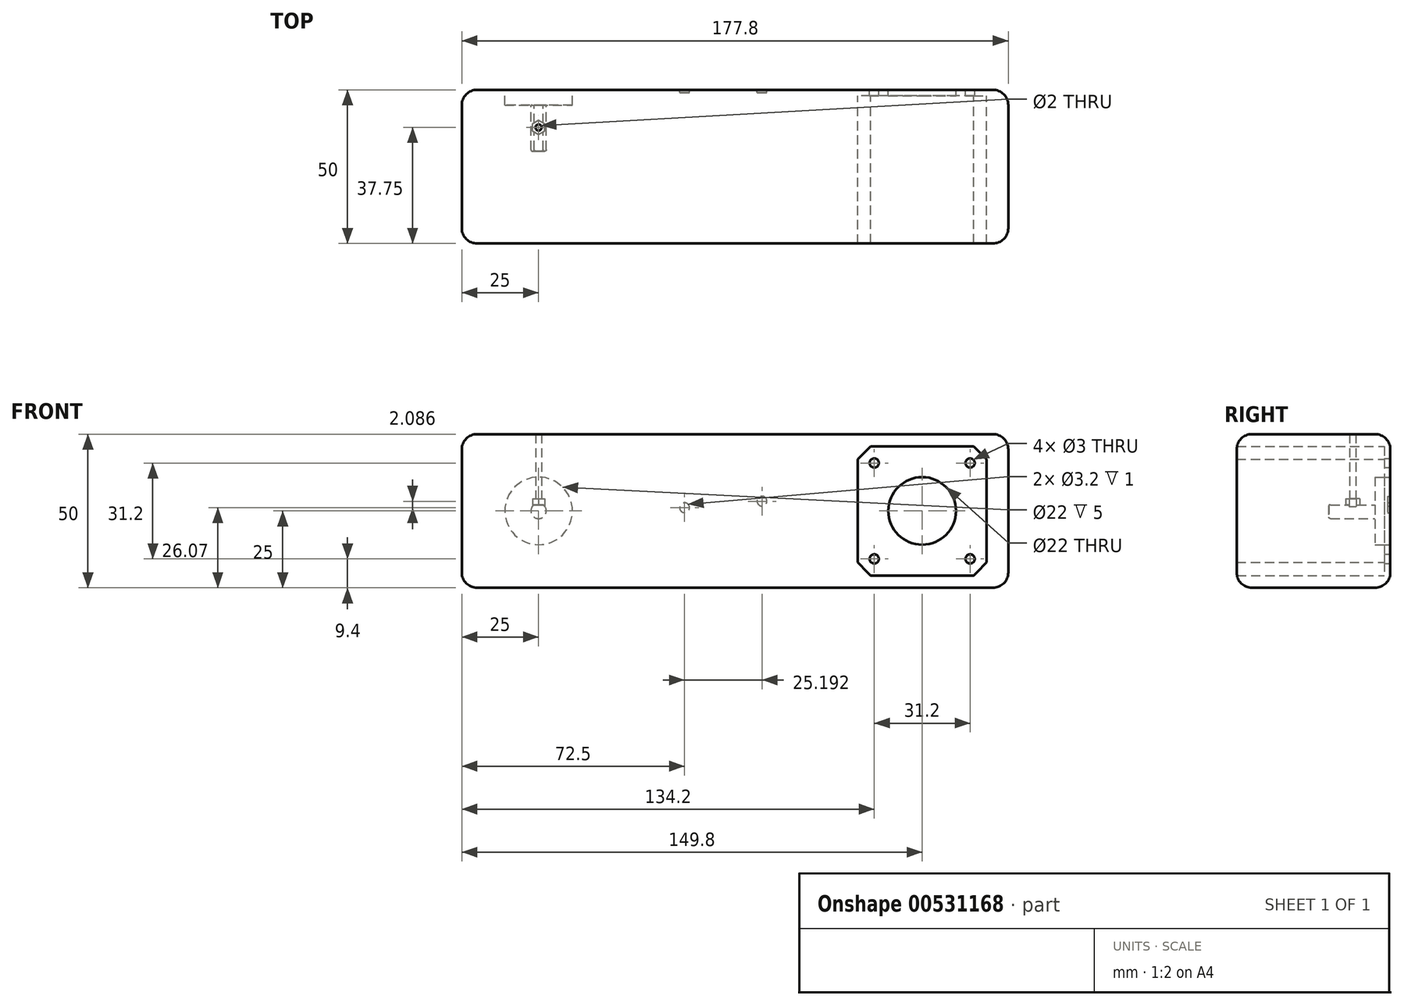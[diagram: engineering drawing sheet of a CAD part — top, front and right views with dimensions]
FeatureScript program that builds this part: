
annotation { "Feature Type Name" : "Feature", "Feature Type Description" : "" }
export const myFeature = defineFeature(function(context is Context, id is Id, definition is map)
    precondition{}
    {
        {
            var Q0;
            Q0=qCreatedBy(makeId("Front.planeOp"),FACE);
            var sketch = newSketch(context, id + "F0", { "sketchPlane" : qUnion([Q0])});
            skLineSegment(sketch, "E0.bottom", {"start": v(-88.9, -25) * mm, "end": v(88.9, -25) * mm});
            skLineSegment(sketch, "E0.top", {"start": v(-88.9, 25) * mm, "end": v(88.9, 25) * mm});
            skLineSegment(sketch, "E0.left", {"start": v(-88.9, -25) * mm, "end": v(-88.9, 25) * mm});
            skLineSegment(sketch, "E0.right", {"start": v(88.9, -25) * mm, "end": v(88.9, 25) * mm});
            skPoint(sketch, "E0.middle", {"position": v(0, 0) * mm});
            skSolve(sketch);
        }
        {
            var Q0;
            Q0 = qSketchRegion(id + "F0", true);
            extrude(context, id + "F1", {"entities" : qUnion([Q0]), "depth" : 50 * mm, "offsetDistance" : 25 * mm});
        }
        {
            var Q0;
            Q0=makeQuery(id+"F1.opExtrude","CAP_FACE",FACE,{"disambiguationData":[OSD([sQuery(id+"F0.wireOp",EDGE,"E0.bottom"),sQuery(id+"F0.wireOp",EDGE,"E0.top"),sQuery(id+"F0.wireOp",EDGE,"E0.left"),sQuery(id+"F0.wireOp",EDGE,"E0.right")])],"isStart":true});
            var sketch = newSketch(context, id + "F2", { "sketchPlane" : qUnion([Q0])});
            skPoint(sketch, "E1.middle", {"position": v(-60.9, 0) * mm});
            skLineSegment(sketch, "E2", {"start": v(-77.66, 21) * mm, "end": v(-81.9, 16.76) * mm});
            skLineSegment(sketch, "E3", {"start": v(-77.66, 21) * mm, "end": v(-44.14, 21) * mm});
            skLineSegment(sketch, "E4", {"start": v(-44.14, 21) * mm, "end": v(-39.9, 16.76) * mm});
            skLineSegment(sketch, "E5", {"start": v(-81.9, 16.76) * mm, "end": v(-81.9, -16.76) * mm});
            skLineSegment(sketch, "E6", {"start": v(-81.9, -16.76) * mm, "end": v(-77.66, -21) * mm});
            skLineSegment(sketch, "E7", {"start": v(-77.66, -21) * mm, "end": v(-44.14, -21) * mm});
            skLineSegment(sketch, "E8", {"start": v(-44.14, -21) * mm, "end": v(-39.9, -16.76) * mm});
            skLineSegment(sketch, "E9", {"start": v(-39.9, -16.76) * mm, "end": v(-39.9, 16.76) * mm});
            skLineSegment(sketch, "E10", {"start": v(-60.9, 0) * mm, "end": v(-60.9, -21) * mm, "construction": true});
            skLineSegment(sketch, "E11", {"start": v(-60.9, 0) * mm, "end": v(-39.9, 0) * mm, "construction": true});
            skLineSegment(sketch, "E12", {"start": v(-60.9, 0) * mm, "end": v(-81.9, 0) * mm, "construction": true});
            skLineSegment(sketch, "E13", {"start": v(-60.9, 0) * mm, "end": v(-60.9, 21) * mm, "construction": true});
            skLineSegment(sketch, "E14.bottom", {"start": v(-76.5, -15.6) * mm, "end": v(-76.5, 15.6) * mm});
            skLineSegment(sketch, "E14.top", {"start": v(-45.3, -15.6) * mm, "end": v(-45.3, 15.6) * mm});
            skLineSegment(sketch, "E14.left", {"start": v(-76.5, -15.6) * mm, "end": v(-45.3, -15.6) * mm});
            skLineSegment(sketch, "E14.right", {"start": v(-76.5, 15.6) * mm, "end": v(-45.3, 15.6) * mm});
            skCircle(sketch, "E15", {"center": v(-45.3, 15.6) * mm, "radius": 1.5 * mm});
            skCircle(sketch, "E16", {"center": v(-45.3, -15.6) * mm, "radius": 1.5 * mm});
            skCircle(sketch, "E17", {"center": v(-76.5, -15.6) * mm, "radius": 1.5 * mm});
            skCircle(sketch, "E18", {"center": v(-76.5, 15.6) * mm, "radius": 1.5 * mm});
            skLineSegment(sketch, "E19.bottom", {"start": v(-39.9, 8.1) * mm, "end": v(-39.9, -8.1) * mm});
            skLineSegment(sketch, "E19.top", {"start": v(-27.9, 8.1) * mm, "end": v(-27.9, -8.1) * mm});
            skLineSegment(sketch, "E19.left", {"start": v(-39.9, 8.1) * mm, "end": v(-27.9, 8.1) * mm});
            skLineSegment(sketch, "E19.right", {"start": v(-39.9, -8.1) * mm, "end": v(-27.9, -8.1) * mm});
            skLineSegment(sketch, "E20", {"start": v(-39.9, -8.1) * mm, "end": v(-39.9, -16.76) * mm, "construction": true});
            skLineSegment(sketch, "E21", {"start": v(-39.9, 8.1) * mm, "end": v(-39.9, 16.76) * mm, "construction": true});
            skLineSegment(sketch, "E22", {"start": v(-77.66, 21) * mm, "end": v(-77.66, 25) * mm, "construction": true});
            skLineSegment(sketch, "E23", {"start": v(-77.66, -21) * mm, "end": v(-77.66, -25) * mm, "construction": true});
            skLineSegment(sketch, "E24", {"start": v(-81.9, -16.76) * mm, "end": v(-88.9, -16.76) * mm, "construction": true});
            skSolve(sketch);
        }
        {
            var Q0;
            Q0=makeQuery(id+"F2.imprint","IMPRINT",FACE,{"disambiguationData":[TD([[makeQuery(id+"F2.imprint","IMPRINT",EDGE,{"derivedFrom":sQuery(id+"F2.wireOp",EDGE,"E2")}),1.0]])]});
            var Q1;
            {var subQ5=sQuery(id+"F2.wireOp",EDGE,"E17");var subQ10=sQuery(id+"F2.wireOp",EDGE,"E14.bottom");var subQ15=makeQuery(id+"F2.imprint","INTERSECT",VERTEX,{"derivedFrom":[subQ10,subQ5]});Q1=makeQuery(id+"F2.imprint","IMPRINT",FACE,{"disambiguationData":[TD([[makeQuery(id+"F2.imprint","IMPRINT",EDGE,{"disambiguationData":[TD([[subQ15,-1.0]])],"derivedFrom":subQ10}),-1.0]])]});}
            var Q2;
            Q2=makeQuery(id+"F2.imprint","IMPRINT",FACE,{"disambiguationData":[TD([[makeQuery(id+"F2.imprint","IMPRINT",EDGE,{"derivedFrom":sQuery(id+"F2.wireOp",EDGE,"E19.bottom")}),1.0]])]});
            var Q3;
            {var subQ0=sQuery(id+"F2.wireOp",EDGE,"E14.right");var subQ1=sQuery(id+"F2.wireOp",EDGE,"E14.top");var subQ2=makeQuery(id+"F2.imprint","INTERSECT",VERTEX,{"derivedFrom":[subQ1,subQ0]});Q3=makeQuery(id+"F2.imprint","IMPRINT",FACE,{"disambiguationData":[TD([[makeQuery(id+"F2.imprint","IMPRINT",EDGE,{"disambiguationData":[TD([[subQ2,1.0]])],"derivedFrom":subQ1}),-1.0]])]});}
            var Q4;
            {var subQ0=sQuery(id+"F2.wireOp",EDGE,"E14.right");var subQ1=sQuery(id+"F2.wireOp",EDGE,"E14.top");var subQ2=makeQuery(id+"F2.imprint","INTERSECT",VERTEX,{"derivedFrom":[subQ1,subQ0]});Q4=makeQuery(id+"F2.imprint","IMPRINT",FACE,{"disambiguationData":[TD([[makeQuery(id+"F2.imprint","IMPRINT",EDGE,{"disambiguationData":[TD([[subQ2,1.0]])],"derivedFrom":subQ1}),1.0]])]});}
            var Q5;
            {var subQ0=sQuery(id+"F2.wireOp",EDGE,"E14.left");var subQ1=sQuery(id+"F2.wireOp",EDGE,"E14.top");var subQ2=makeQuery(id+"F2.imprint","INTERSECT",VERTEX,{"derivedFrom":[subQ1,subQ0]});Q5=makeQuery(id+"F2.imprint","IMPRINT",FACE,{"disambiguationData":[TD([[makeQuery(id+"F2.imprint","IMPRINT",EDGE,{"disambiguationData":[TD([[subQ2,-1.0]])],"derivedFrom":subQ1}),1.0]])]});}
            var Q6;
            {var subQ0=sQuery(id+"F2.wireOp",EDGE,"E14.left");var subQ1=sQuery(id+"F2.wireOp",EDGE,"E14.top");var subQ2=makeQuery(id+"F2.imprint","INTERSECT",VERTEX,{"derivedFrom":[subQ1,subQ0]});Q6=makeQuery(id+"F2.imprint","IMPRINT",FACE,{"disambiguationData":[TD([[makeQuery(id+"F2.imprint","IMPRINT",EDGE,{"disambiguationData":[TD([[subQ2,-1.0]])],"derivedFrom":subQ1}),-1.0]])]});}
            var Q7;
            {var subQ0=sQuery(id+"F2.wireOp",EDGE,"E14.left");var subQ1=sQuery(id+"F2.wireOp",EDGE,"E14.bottom");var subQ2=makeQuery(id+"F2.imprint","INTERSECT",VERTEX,{"derivedFrom":[subQ1,subQ0]});Q7=makeQuery(id+"F2.imprint","IMPRINT",FACE,{"disambiguationData":[TD([[makeQuery(id+"F2.imprint","IMPRINT",EDGE,{"disambiguationData":[TD([[subQ2,-1.0]])],"derivedFrom":subQ1}),1.0]])]});}
            var Q8;
            {var subQ0=sQuery(id+"F2.wireOp",EDGE,"E14.left");var subQ1=sQuery(id+"F2.wireOp",EDGE,"E14.bottom");var subQ2=makeQuery(id+"F2.imprint","INTERSECT",VERTEX,{"derivedFrom":[subQ1,subQ0]});Q8=makeQuery(id+"F2.imprint","IMPRINT",FACE,{"disambiguationData":[TD([[makeQuery(id+"F2.imprint","IMPRINT",EDGE,{"disambiguationData":[TD([[subQ2,-1.0]])],"derivedFrom":subQ1}),-1.0]])]});}
            var Q9;
            {var subQ0=sQuery(id+"F2.wireOp",EDGE,"E14.right");var subQ1=sQuery(id+"F2.wireOp",EDGE,"E14.bottom");var subQ2=makeQuery(id+"F2.imprint","INTERSECT",VERTEX,{"derivedFrom":[subQ1,subQ0]});Q9=makeQuery(id+"F2.imprint","IMPRINT",FACE,{"disambiguationData":[TD([[makeQuery(id+"F2.imprint","IMPRINT",EDGE,{"disambiguationData":[TD([[subQ2,1.0]])],"derivedFrom":subQ1}),-1.0]])]});}
            var Q10;
            {var subQ0=sQuery(id+"F2.wireOp",EDGE,"E14.right");var subQ1=sQuery(id+"F2.wireOp",EDGE,"E14.bottom");var subQ2=makeQuery(id+"F2.imprint","INTERSECT",VERTEX,{"derivedFrom":[subQ1,subQ0]});Q10=makeQuery(id+"F2.imprint","IMPRINT",FACE,{"disambiguationData":[TD([[makeQuery(id+"F2.imprint","IMPRINT",EDGE,{"disambiguationData":[TD([[subQ2,1.0]])],"derivedFrom":subQ1}),1.0]])]});}
            extrude(context, id + "F3", {"entities" : qUnion([Q0, Q1, Q2, Q3, Q4, Q5, Q6, Q7, Q8, Q9, Q10]), "operationType" : NewBodyOperationType.REMOVE, "endBound" : BoundingType.UP_TO_NEXT, "oppositeDirection" : true, "depth" : 40 * mm, "offsetDistance" : 25 * mm});
        }
        {
            var Q0;
            Q0=makeQuery(id+"F1.opExtrude","CAP_FACE",FACE,{"disambiguationData":[OSD([sQuery(id+"F0.wireOp",EDGE,"E0.bottom"),sQuery(id+"F0.wireOp",EDGE,"E0.top"),sQuery(id+"F0.wireOp",EDGE,"E0.left"),sQuery(id+"F0.wireOp",EDGE,"E0.right")])],"isStart":true});
            var sketch = newSketch(context, id + "F4", { "sketchPlane" : qUnion([Q0])});
            skCircle(sketch, "E25", {"center": v(63.9, 0) * mm, "radius": 11 * mm});
            skSolve(sketch);
        }
        {
            var Q0;
            Q0 = qSketchRegion(id + "F4", true);
            extrude(context, id + "F5", {"entities" : qUnion([Q0]), "operationType" : NewBodyOperationType.REMOVE, "oppositeDirection" : true, "depth" : 5 * mm, "offsetDistance" : 25 * mm});
        }
        {
            var Q0;
            Q0=makeQuery(id+"F5.boolean.opBoolean","COPY",FACE,{"derivedFrom":makeQuery(id+"F5.opExtrude","CAP_FACE",FACE,{"disambiguationData":[OSD([sQuery(id+"F4.wireOp",EDGE,"E25")])],"isStart":false})});
            var sketch = newSketch(context, id + "F6", { "sketchPlane" : qUnion([Q0])});
            skArc(sketch, "E26", {"start": v(62.4, 2) * mm, "mid": v(63.9, -2.5) * mm, "end": v(65.4, 2) * mm});
            skLineSegment(sketch, "E27", {"start": v(62.4, 2) * mm, "end": v(65.4, 2) * mm});
            skSolve(sketch);
        }
        {
            var Q0;
            Q0 = qSketchRegion(id + "F6", true);
            extrude(context, id + "F7", {"entities" : qUnion([Q0]), "operationType" : NewBodyOperationType.REMOVE, "oppositeDirection" : true, "depth" : 15 * mm, "offsetDistance" : 25 * mm});
        }
        {
            var Q0;
            Q0=makeQuery(id+"F7.boolean.opBoolean","COPY",EDGE,{"derivedFrom":makeQuery(id+"F7.opExtrude","CAP_EDGE",EDGE,{"disambiguationData":[OSD([sQuery(id+"F6.wireOp",EDGE,"E26")])],"isStart":false})});
            fillet(context, id + "F8", {"entities" : qUnion([Q0]), "radius" : .5 * mm, "tangentPropagation" : true, "allowEdgeOverflow" : false});
        }
        {
            var Q0;
            Q0=makeQuery(id+"F1.opExtrude","SWEPT_EDGE",EDGE,{"disambiguationData":[OSD([sQuery(id+"F0.wireOp",EDGE,"E0.top"),sQuery(id+"F0.wireOp",EDGE,"E0.left")])]});
            var Q1;
            Q1=makeQuery(id+"F1.opExtrude","CAP_EDGE",EDGE,{"disambiguationData":[OSD([sQuery(id+"F0.wireOp",EDGE,"E0.top")])],"isStart":false});
            var Q2;
            Q2=makeQuery(id+"F1.opExtrude","CAP_EDGE",EDGE,{"disambiguationData":[OSD([sQuery(id+"F0.wireOp",EDGE,"E0.bottom")])],"isStart":false});
            var Q3;
            Q3=makeQuery(id+"F1.opExtrude","CAP_EDGE",EDGE,{"disambiguationData":[OSD([sQuery(id+"F0.wireOp",EDGE,"E0.right")])],"isStart":false});
            var Q4;
            Q4=makeQuery(id+"F1.opExtrude","SWEPT_EDGE",EDGE,{"disambiguationData":[OSD([sQuery(id+"F0.wireOp",EDGE,"E0.top"),sQuery(id+"F0.wireOp",EDGE,"E0.right")])]});
            var Q5;
            Q5=makeQuery(id+"F1.opExtrude","CAP_EDGE",EDGE,{"disambiguationData":[OSD([sQuery(id+"F0.wireOp",EDGE,"E0.right")])],"isStart":true});
            var Q6;
            Q6=makeQuery(id+"F1.opExtrude","CAP_EDGE",EDGE,{"disambiguationData":[OSD([sQuery(id+"F0.wireOp",EDGE,"E0.top")])],"isStart":true});
            var Q7;
            Q7=makeQuery(id+"F1.opExtrude","CAP_EDGE",EDGE,{"disambiguationData":[OSD([sQuery(id+"F0.wireOp",EDGE,"E0.left")])],"isStart":true});
            var Q8;
            Q8=makeQuery(id+"F1.opExtrude","CAP_EDGE",EDGE,{"disambiguationData":[OSD([sQuery(id+"F0.wireOp",EDGE,"E0.bottom")])],"isStart":true});
            var Q9;
            Q9=makeQuery(id+"F1.opExtrude","SWEPT_EDGE",EDGE,{"disambiguationData":[OSD([sQuery(id+"F0.wireOp",EDGE,"E0.bottom"),sQuery(id+"F0.wireOp",EDGE,"E0.left")])]});
            var Q10;
            Q10=makeQuery(id+"F1.opExtrude","CAP_EDGE",EDGE,{"disambiguationData":[OSD([sQuery(id+"F0.wireOp",EDGE,"E0.left")])],"isStart":false});
            var Q11;
            Q11=makeQuery(id+"F1.opExtrude","SWEPT_EDGE",EDGE,{"disambiguationData":[OSD([sQuery(id+"F0.wireOp",EDGE,"E0.bottom"),sQuery(id+"F0.wireOp",EDGE,"E0.right")])]});
            fillet(context, id + "F9", {"entities" : qUnion([Q0, Q1, Q2, Q3, Q4, Q5, Q6, Q7, Q8, Q9, Q10, Q11]), "radius" : 5 * mm, "tangentPropagation" : true, "allowEdgeOverflow" : false});
        }
        {
            var Q0;
            {var subQ0=makeQuery(id+"F1.opExtrude","CAP_FACE",FACE,{"disambiguationData":[OSD([sQuery(id+"F0.wireOp",EDGE,"E0.bottom"),sQuery(id+"F0.wireOp",EDGE,"E0.top"),sQuery(id+"F0.wireOp",EDGE,"E0.left"),sQuery(id+"F0.wireOp",EDGE,"E0.right")])],"isStart":true});Q0=makeQuery(id+"FoZovRg3xTCLnNm_1.boolean.opBoolean","MERGE",FACE,{"derivedFrom":[makeQuery(id+"F9.opFillet","SPLIT",FACE,{"disambiguationData":[OD(0.0)],"derivedFrom":subQ0}),makeQuery(id+"F9.opFillet","SPLIT",FACE,{"disambiguationData":[OD(1.0)],"derivedFrom":subQ0}),makeQuery(id+"F9.opFillet","SPLIT",FACE,{"disambiguationData":[OD(2.0)],"derivedFrom":subQ0}),makeQuery(id+"FoZovRg3xTCLnNm_1.opExtrude","CAP_FACE",FACE,{"disambiguationData":[OSD([sQuery(id+"FDYPuCtW6ixOXja_1.wireOp",EDGE,"YYuf8nkV-7B4A-i0I6-zSbN-53MIC5I7KjFq"),sQuery(id+"FDYPuCtW6ixOXja_1.wireOp",EDGE,"4H2Hm0k3-e9FN-fHA8-mXw3-sr5ssqQ01Vbx"),sQuery(id+"FDYPuCtW6ixOXja_1.wireOp",EDGE,"lZZom5Jz-AmTh-sgkz-kv80-AAgoWgyaM1Zr"),sQuery(id+"FDYPuCtW6ixOXja_1.wireOp",EDGE,"LLcvLUIz-hWV5-o65u-pwfC-TSZD8YiBZfCl"),sQuery(id+"FDYPuCtW6ixOXja_1.wireOp",EDGE,"lBeztXca-4Y93-VHWP-6IyO-vjsOmx6BGO97"),sQuery(id+"FDYPuCtW6ixOXja_1.wireOp",EDGE,"uXL03oxp-f7LO-Q5kk-6GXb-WIKc5kEG4Ux5"),sQuery(id+"FDYPuCtW6ixOXja_1.wireOp",EDGE,"LOLKuHAm-fLqv-NDvD-HPOj-bSX7zAN5uNSS"),sQuery(id+"FDYPuCtW6ixOXja_1.wireOp",EDGE,"BwHCPOQT-nLmt-Bvbi-6YB1-dZPCrpnx4CLv"),sQuery(id+"FDYPuCtW6ixOXja_1.wireOp",EDGE,"jOqzWmFZ-hA5K-doX0-eepj-flvD3r2dRNSL"),sQuery(id+"FDYPuCtW6ixOXja_1.wireOp",EDGE,"f5xZvLuP-w1Fc-xj4t-FIMr-SDlJKQwCImQL"),sQuery(id+"FDYPuCtW6ixOXja_1.wireOp",EDGE,"uXv8KqKA-ETbP-uQs4-SBVH-D6dnb3WF6P8I"),sQuery(id+"FDYPuCtW6ixOXja_1.wireOp",EDGE,"TpemvIDa-usmC-fJeC-MmGX-2MZsz92HwUE6"),sQuery(id+"FDYPuCtW6ixOXja_1.wireOp",EDGE,"ue2nGoUu-wROv-G1DW-kLQD-xeC6K69mbqnW")])],"isStart":true})]});}
            var sketch = newSketch(context, id + "F10", { "sketchPlane" : qUnion([Q0])});
            skCircle(sketch, "E28", {"center": v(16.4, 1.07) * mm, "radius": 1.6 * mm});
            skCircle(sketch, "E29", {"center": v(-8.8, 3.16) * mm, "radius": 1.6 * mm});
            skLineSegment(sketch, "E30.left", {"start": v(17.65, 3.24) * mm, "end": v(-2.15, 14.67) * mm});
            skLineSegment(sketch, "E30.right", {"start": v(9.75, -10.44) * mm, "end": v(-10.04, 1) * mm});
            skLineSegment(sketch, "E31", {"start": v(18.57, -0.18) * mm, "end": v(13.17, -9.52) * mm});
            skLineSegment(sketch, "E32", {"start": v(-5.56, 13.75) * mm, "end": v(-10.96, 4.4) * mm});
            skArc(sketch, "E33", {"start": v(18.57, -0.18) * mm, "mid": v(18.81, 1.72) * mm, "end": v(17.65, 3.24) * mm});
            skArc(sketch, "E34", {"start": v(9.75, -10.44) * mm, "mid": v(11.65, -10.69) * mm, "end": v(13.17, -9.52) * mm});
            skArc(sketch, "E35", {"start": v(-2.15, 14.67) * mm, "mid": v(-4.04, 14.91) * mm, "end": v(-5.56, 13.75) * mm});
            skArc(sketch, "E36", {"start": v(-10.96, 4.4) * mm, "mid": v(-11.2, 2.5) * mm, "end": v(-10.04, 1) * mm});
            skSolve(sketch);
        }
        {
            var Q0;
            Q0=makeQuery(id+"F10.imprint","IMPRINT",FACE,{"disambiguationData":[TD([[makeQuery(id+"F10.imprint","IMPRINT",EDGE,{"derivedFrom":sQuery(id+"F10.wireOp",EDGE,"E28")}),1.0]])]});
            var Q1;
            Q1=makeQuery(id+"F10.imprint","IMPRINT",FACE,{"disambiguationData":[TD([[makeQuery(id+"F10.imprint","IMPRINT",EDGE,{"derivedFrom":sQuery(id+"F10.wireOp",EDGE,"E29")}),1.0]])]});
            extrude(context, id + "F11", {"entities" : qUnion([Q0, Q1]), "operationType" : NewBodyOperationType.REMOVE, "oppositeDirection" : true, "depth" : 1 * mm, "offsetDistance" : 25 * mm});
        }
        {
            var Q0;
            Q0=makeQuery(id+"F7.boolean.opBoolean","COPY",FACE,{"derivedFrom":makeQuery(id+"F7.opExtrude","SWEPT_FACE",FACE,{"disambiguationData":[OSD([sQuery(id+"F6.wireOp",EDGE,"E27")])]})});
            var sketch = newSketch(context, id + "F12", { "sketchPlane" : qUnion([Q0])});
            skCircle(sketch, "E37", {"center": v(-63.9, 12.25) * mm, "radius": 1 * mm});
            skLineSegment(sketch, "E38", {"start": v(-63.9, 5) * mm, "end": v(-63.9, 19.5) * mm, "construction": true});
            skCircle(sketch, "E39.cCircle", {"center": v(-63.9, 12.25) * mm, "radius": 2 * mm, "construction": true});
            skLineSegment(sketch, "E39.0", {"start": v(-63.9, 14.56) * mm, "end": v(-61.9, 13.4) * mm});
            skLineSegment(sketch, "E39.1", {"start": v(-61.9, 13.4) * mm, "end": v(-61.9, 11.1) * mm});
            skLineSegment(sketch, "E39.2", {"start": v(-61.9, 11.1) * mm, "end": v(-63.9, 9.94) * mm});
            skLineSegment(sketch, "E39.3", {"start": v(-63.9, 9.94) * mm, "end": v(-65.9, 11.1) * mm});
            skLineSegment(sketch, "E39.4", {"start": v(-65.9, 11.1) * mm, "end": v(-65.9, 13.4) * mm});
            skLineSegment(sketch, "E39.5", {"start": v(-65.9, 13.4) * mm, "end": v(-63.9, 14.56) * mm});
            skPoint(sketch, "E39.0.midPoint", {"position": v(-62.9, 13.98) * mm});
            skSolve(sketch);
        }
        {
            var Q0;
            Q0 = qSketchRegion(id + "F12", true);
            extrude(context, id + "F13", {"entities" : qUnion([Q0]), "operationType" : NewBodyOperationType.REMOVE, "oppositeDirection" : true, "depth" : 2 * mm, "offsetDistance" : 25 * mm, "hasSecondDirection" : true, "secondDirectionOppositeDirection" : false, "secondDirectionDepth" : 1 * mm});
        }
        {
            var Q0;
            Q0=makeQuery(id+"F12.imprint","IMPRINT",FACE,{"disambiguationData":[TD([[makeQuery(id+"F12.imprint","IMPRINT",EDGE,{"derivedFrom":sQuery(id+"F12.wireOp",EDGE,"E37")}),1.0]])]});
            extrude(context, id + "F14", {"entities" : qUnion([Q0]), "operationType" : NewBodyOperationType.REMOVE, "oppositeDirection" : true, "depth" : 25 * mm, "offsetDistance" : 25 * mm});
        }
        {
            var Q0;
            Q0=makeQuery(id+"F2.imprint","IMPRINT",FACE,{"disambiguationData":[TD([[makeQuery(id+"F2.imprint","IMPRINT",EDGE,{"derivedFrom":sQuery(id+"F2.wireOp",EDGE,"E2")}),1.0]])]});
            var Q1;
            Q1=makeQuery(id+"F2.imprint","IMPRINT",FACE,{"disambiguationData":[TD([[makeQuery(id+"F2.imprint","IMPRINT",EDGE,{"derivedFrom":sQuery(id+"F2.wireOp",EDGE,"E19.bottom")}),1.0]])]});
            var Q2;
            {var subQ5=sQuery(id+"F2.wireOp",EDGE,"E17");var subQ10=sQuery(id+"F2.wireOp",EDGE,"E14.bottom");var subQ15=makeQuery(id+"F2.imprint","INTERSECT",VERTEX,{"derivedFrom":[subQ10,subQ5]});Q2=makeQuery(id+"F2.imprint","IMPRINT",FACE,{"disambiguationData":[TD([[makeQuery(id+"F2.imprint","IMPRINT",EDGE,{"disambiguationData":[TD([[subQ15,-1.0]])],"derivedFrom":subQ10}),-1.0]])]});}
            extrude(context, id + "F15", {"entities" : qUnion([Q0, Q1, Q2]), "operationType" : NewBodyOperationType.ADD, "oppositeDirection" : true, "depth" : 2 * mm, "offsetDistance" : 25 * mm});
        }
        {
            var Q0;
            {var subQ5=sQuery(id+"F2.wireOp",EDGE,"E17");var subQ10=sQuery(id+"F2.wireOp",EDGE,"E14.bottom");var subQ15=makeQuery(id+"F2.imprint","INTERSECT",VERTEX,{"derivedFrom":[subQ10,subQ5]});Q0=makeQuery(id+"F2.imprint","IMPRINT",FACE,{"disambiguationData":[TD([[makeQuery(id+"F2.imprint","IMPRINT",EDGE,{"disambiguationData":[TD([[subQ15,-1.0]])],"derivedFrom":subQ10}),-1.0]])]});}
            var sketch = newSketch(context, id + "F16", { "sketchPlane" : qUnion([Q0])});
            skCircle(sketch, "E40", {"center": v(-60.9, 0) * mm, "radius": 11 * mm});
            skSolve(sketch);
        }
        {
            var Q0;
            Q0 = qSketchRegion(id + "F16", true);
            extrude(context, id + "F17", {"entities" : qUnion([Q0]), "operationType" : NewBodyOperationType.REMOVE, "oppositeDirection" : true, "depth" : 25 * mm, "offsetDistance" : 25 * mm});
        }
    });
